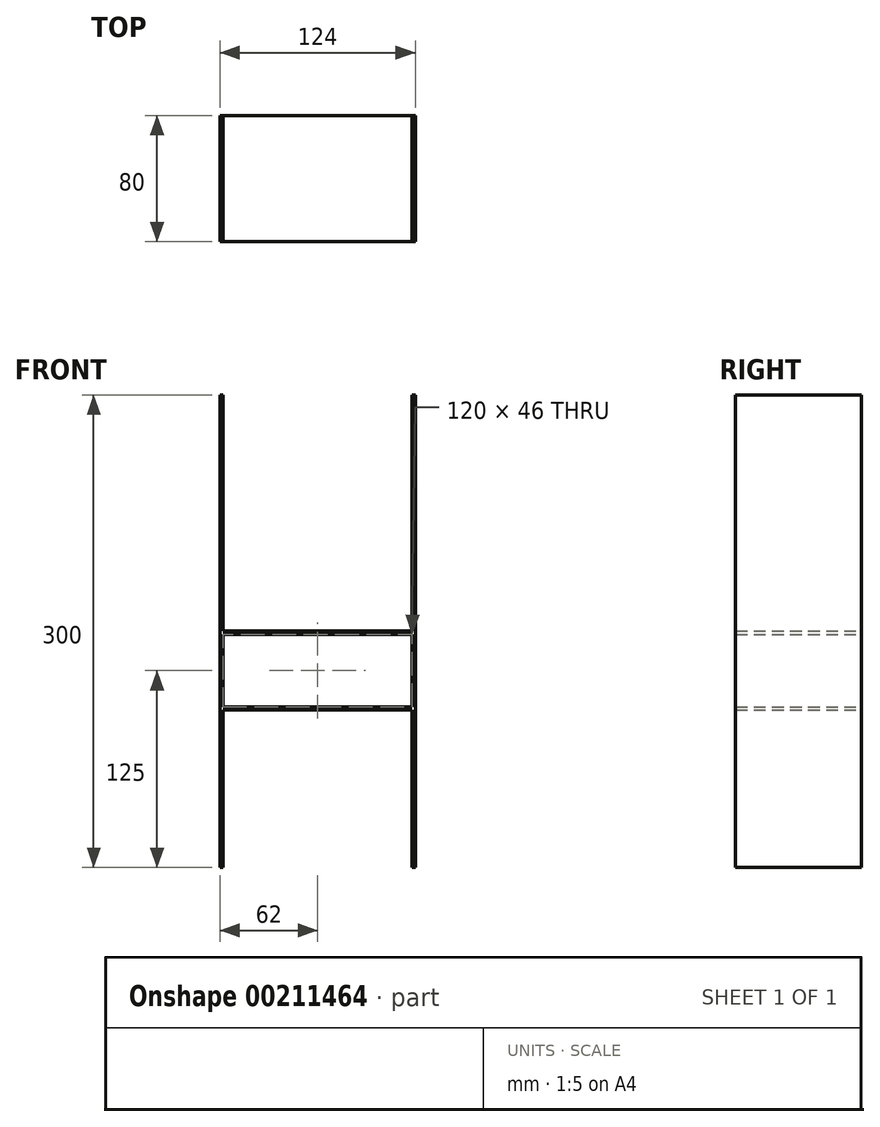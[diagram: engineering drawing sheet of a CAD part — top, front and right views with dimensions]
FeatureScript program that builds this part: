
annotation { "Feature Type Name" : "Feature", "Feature Type Description" : "" }
export const myFeature = defineFeature(function(context is Context, id is Id, definition is map)
    precondition{}
    {
        {
            var Q0;
            Q0=qCreatedBy(makeId("Front.planeOp"),FACE);
            var sketch = newSketch(context, id + "F0", { "sketchPlane" : qUnion([Q0])});
            skLineSegment(sketch, "E0", {"start": v(0, -55.06) * mm, "end": v(0, 55.06) * mm, "construction": true});
            skLineSegment(sketch, "E1", {"start": v(-60, 0) * mm, "end": v(60, 0) * mm});
            skLineSegment(sketch, "E2", {"start": v(60, 0) * mm, "end": v(60, 150) * mm});
            skLineSegment(sketch, "E3", {"start": v(60, 150) * mm, "end": v(62, 150) * mm});
            skLineSegment(sketch, "E4", {"start": v(62, 150) * mm, "end": v(62, -150) * mm});
            skLineSegment(sketch, "E5", {"start": v(62, -150) * mm, "end": v(60, -150) * mm});
            skLineSegment(sketch, "E6", {"start": v(60, -150) * mm, "end": v(60, -50) * mm});
            skLineSegment(sketch, "E7", {"start": v(60, -50) * mm, "end": v(-60, -50) * mm});
            skLineSegment(sketch, "E8", {"start": v(-60, -50) * mm, "end": v(-60, -150) * mm});
            skLineSegment(sketch, "E9", {"start": v(-60, -150) * mm, "end": v(-62, -150) * mm});
            skLineSegment(sketch, "E10", {"start": v(60, -2) * mm, "end": v(-60, -2) * mm});
            skLineSegment(sketch, "E11", {"start": v(-60, -2) * mm, "end": v(-60, -48) * mm});
            skLineSegment(sketch, "E12", {"start": v(-60, -48) * mm, "end": v(60, -48) * mm});
            skLineSegment(sketch, "E13", {"start": v(60, -48) * mm, "end": v(60, -2) * mm});
            skLineSegment(sketch, "E14", {"start": v(-62, -150) * mm, "end": v(-62, 150) * mm});
            skLineSegment(sketch, "E15", {"start": v(-62, 150) * mm, "end": v(-60, 150) * mm});
            skLineSegment(sketch, "E16", {"start": v(-60, 150) * mm, "end": v(-60, 0) * mm});
            skSolve(sketch);
        }
        {
            var Q0;
            Q0=qSketchRegion(id+"F0",true);
            extrude(context, id + "F1", {"entities" : qUnion([Q0]), "depth" : 80 * mm, "symmetric" : true});
        }
    });
